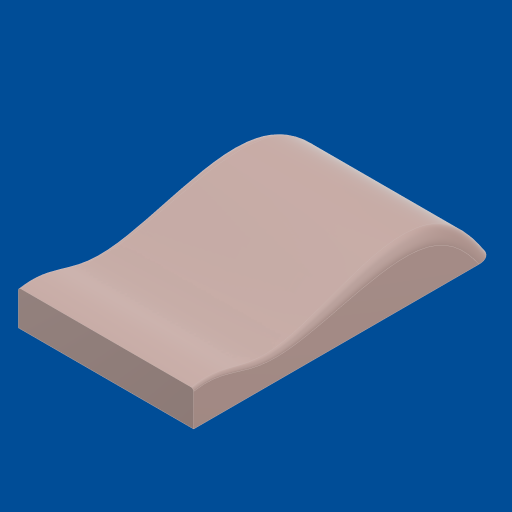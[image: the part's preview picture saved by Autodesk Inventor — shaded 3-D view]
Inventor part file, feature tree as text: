
AUTODESK INVENTOR PART (.ipt)
format: ipt  version: 2023.1 (Build 271208000, 208)  size: 260,096 bytes
history: native  units: mm
features: fillet x4, sketch x3, other x1, extrude x1, split x1, shell x1
ambient origin geometry x8: Origin, YZ Plane, XZ Plane, XY Plane, X Axis, Y Axis, Z Axis, Center Point
bodies: Solid1 (feature_tree)
feature tree (11):
  other  "top_case.ipt"
  extrude  "Extrusion1"  Depth=30.0mm TaperAngle=0.0deg
  split  "Split1"
  shell  "Shell1"  Thickness=1.0mm
  fillet  "Fillet1"  Radius=5.0mm
  fillet  "Fillet2"  Radius=1.0mm
  fillet  "Fillet3"  [1 undecoded]
  fillet  "Fillet4"  [1 undecoded]
  sketch  "Sketch9"  dims[d5=2.0mm d6=5.0mm d7=5.0mm d8=1.0mm d9=5.0mm d10=1.0mm d11=1.0mm d12=5.0mm]
  sketch  "Sketch10"
  sketch  "Sketch3"  dims[d0=10.0mm d1=30.0mm d2=0.0mm d3=1.0mm]
note: 2 required parameter values undecoded (feature->parameter linkage not recoverable at this tier; creation-order binding heuristic only, values carry confidence <= 0.55)
